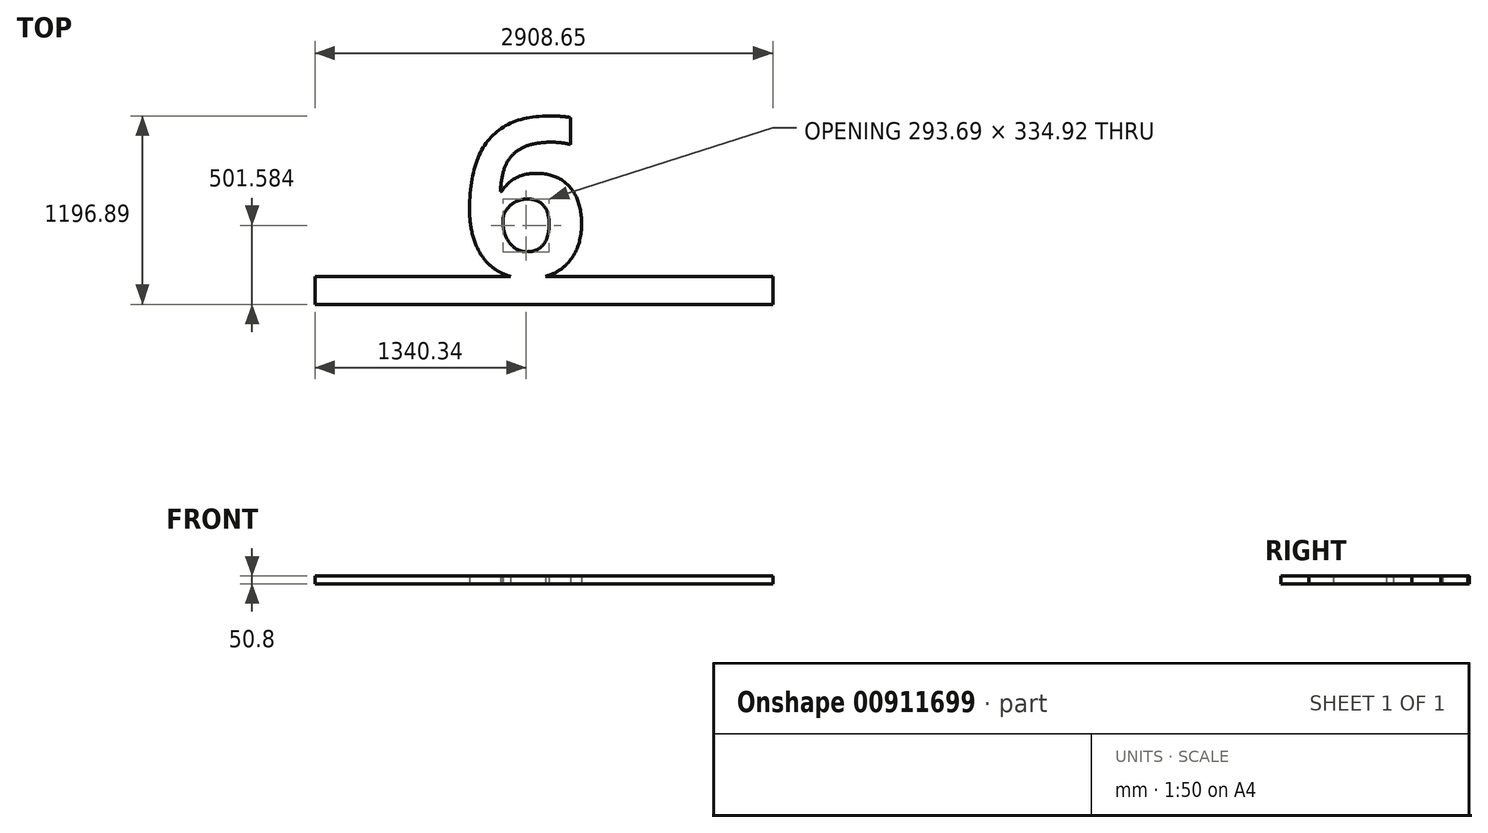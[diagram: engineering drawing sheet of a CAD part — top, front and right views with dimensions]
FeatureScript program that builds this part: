
annotation { "Feature Type Name" : "Feature", "Feature Type Description" : "" }
export const myFeature = defineFeature(function(context is Context, id is Id, definition is map)
    precondition{}
    {
        {
            var Q0;
            Q0=qCreatedBy(makeId("Top.planeOp"),FACE);
            var sketch = newSketch(context, id + "F0", { "sketchPlane" : qUnion([Q0])});
            skLineSegment(sketch, "E0.bottom", {"start": v(-275.51, -177.8) * mm, "end": v(2633.14, -177.8) * mm});
            skLineSegment(sketch, "E0.top", {"start": v(-275.51, 0) * mm, "end": v(2633.14, 0) * mm});
            skLineSegment(sketch, "E0.left", {"start": v(-275.51, -177.8) * mm, "end": v(-275.51, 0) * mm});
            skLineSegment(sketch, "E0.right", {"start": v(2633.14, -177.8) * mm, "end": v(2633.14, 0) * mm});
            skText(sketch, "E1", { "text": "16H", "fontName": "OpenSans-Bold.ttf"});
            const initialGuessF0  = {"E1": [-0.14851, 0, 1, 0, 1.016]};
            skSetInitialGuess(sketch, initialGuessF0);
            skSolve(sketch);
        }
        {
            var Q0;
            Q0=makeQuery(id+"F0.imprint","IMPRINT",FACE,{"disambiguationData":[TD([[makeQuery(id+"F0.imprint","IMPRINT",EDGE,{"derivedFrom":sQuery(id+"F0.wireOp",EDGE,"E1.sketch_text.stroke-10")}),-1.0]])]});
            var Q1;
            {var subQ0=sQuery(id+"F0.wireOp",EDGE,"E1.sketch_text.stroke-24");var subQ1=sQuery(id+"F0.wireOp",EDGE,"E0.top");var subQ2=makeQuery(id+"F0.imprint","INTERSECT",VERTEX,{"derivedFrom":[subQ1,subQ0]});Q1=makeQuery(id+"F0.imprint","IMPRINT",FACE,{"disambiguationData":[TD([[makeQuery(id+"F0.imprint","IMPRINT",EDGE,{"disambiguationData":[TD([[subQ2,-1.0]])],"derivedFrom":subQ1}),-1.0]])]});}
            var Q2;
            Q2=makeQuery(id+"F0.imprint","IMPRINT",FACE,{"disambiguationData":[TD([[makeQuery(id+"F0.imprint","IMPRINT",EDGE,{"derivedFrom":sQuery(id+"F0.wireOp",EDGE,"E0.bottom")}),1.0]])]});
            var Q3;
            Q3=makeQuery(id+"F0.imprint","IMPRINT",FACE,{"disambiguationData":[TD([[makeQuery(id+"F0.imprint","IMPRINT",EDGE,{"derivedFrom":sQuery(id+"F0.wireOp",EDGE,"E1.sketch_text.stroke-0")}),-1.0]])]});
            var Q4;
            Q4=makeQuery(id+"F0.imprint","IMPRINT",FACE,{"disambiguationData":[TD([[makeQuery(id+"F0.imprint","IMPRINT",EDGE,{"derivedFrom":sQuery(id+"F0.wireOp",EDGE,"E1.sketch_text.stroke-35")}),-1.0]])]});
            extrude(context, id + "F1", {"entities" : qUnion([Q0, Q1, Q2, Q3, Q4]), "depth" : 50.8 * mm, "offsetDistance" : 25.4 * mm});
        }
    });
